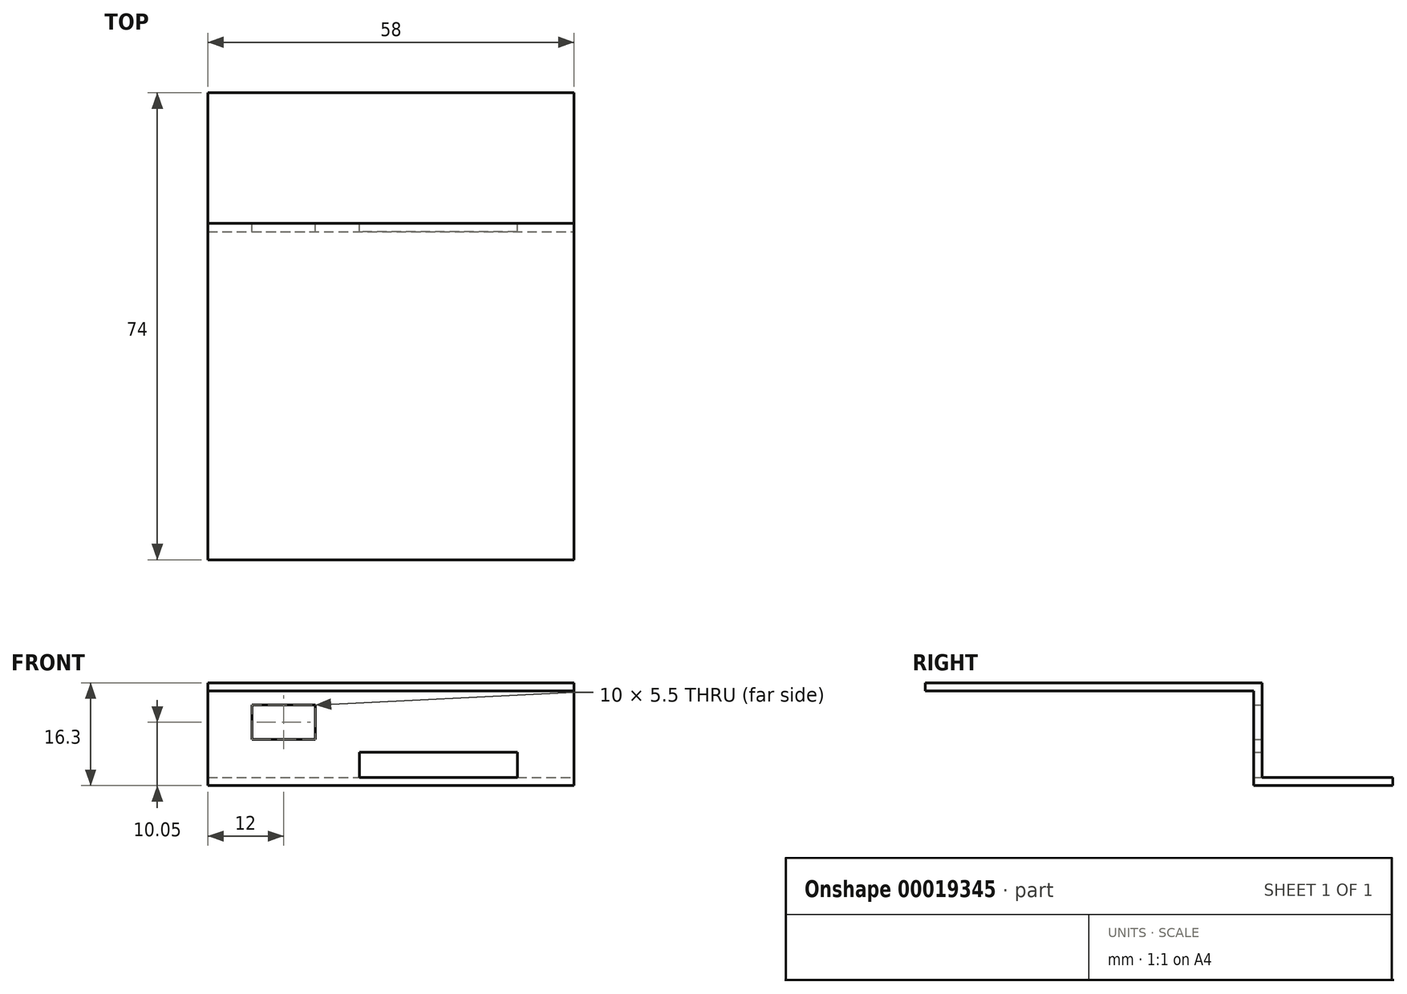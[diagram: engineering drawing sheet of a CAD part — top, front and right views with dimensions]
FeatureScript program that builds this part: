
annotation { "Feature Type Name" : "Feature", "Feature Type Description" : "" }
export const myFeature = defineFeature(function(context is Context, id is Id, definition is map)
    precondition{}
    {
        {
            var Q0;
            Q0=qCreatedBy(makeId("Top.planeOp"),FACE);
            var sketch = newSketch(context, id + "F0", { "sketchPlane" : qUnion([Q0])});
            skLineSegment(sketch, "E0.rect.bottom", {"start": v(27.5, 35.5) * mm, "end": v(-27.5, 35.5) * mm});
            skLineSegment(sketch, "E0.rect.top", {"start": v(27.5, -35.5) * mm, "end": v(-27.5, -35.5) * mm});
            skLineSegment(sketch, "E0.rect.left", {"start": v(27.5, 35.5) * mm, "end": v(27.5, -35.5) * mm});
            skLineSegment(sketch, "E0.rect.right", {"start": v(-27.5, 35.5) * mm, "end": v(-27.5, -35.5) * mm});
            skPoint(sketch, "E0.rect.middle", {"position": v(0, 0) * mm});
            skSolve(sketch);
        }
        {
            var Q0;
            Q0=qCreatedBy(makeId("Top.planeOp"),FACE);
            var sketch = newSketch(context, id + "F1", { "sketchPlane" : qUnion([Q0])});
            skLineSegment(sketch, "E1.0", {"start": v(29, -37) * mm, "end": v(29, 37) * mm});
            skLineSegment(sketch, "E1.1", {"start": v(-29, -37) * mm, "end": v(29, -37) * mm});
            skLineSegment(sketch, "E1.2", {"start": v(-29, 37) * mm, "end": v(-29, -37) * mm});
            skLineSegment(sketch, "E1.3", {"start": v(29, 37) * mm, "end": v(-29, 37) * mm});
            skSolve(sketch);
        }
        {
            var Q0;
            Q0=qSketchRegion(id+"F1",true);
            extrude(context, id + "F2", {"entities" : qUnion([Q0]), "depth" : 32 * mm});
        }
        {
            var Q0;
            Q0=makeQuery(id+"F2.opExtrude","CAP_FACE",FACE,{"disambiguationData":[OSD([sQuery(id+"F1.wireOp",EDGE,"E1.0"),sQuery(id+"F1.wireOp",EDGE,"E1.1"),sQuery(id+"F1.wireOp",EDGE,"E1.2"),sQuery(id+"F1.wireOp",EDGE,"E1.3")])],"isStart":false});
            var sketch = newSketch(context, id + "F3", { "sketchPlane" : qUnion([Q0])});
            skLineSegment(sketch, "E2.0", {"start": v(-27.5, -35.5) * mm, "end": v(27.5, -35.5) * mm});
            skLineSegment(sketch, "E2.1", {"start": v(-27.5, 35.5) * mm, "end": v(-27.5, -35.5) * mm});
            skLineSegment(sketch, "E2.2", {"start": v(27.5, 35.5) * mm, "end": v(-27.5, 35.5) * mm});
            skLineSegment(sketch, "E2.3", {"start": v(27.5, -35.5) * mm, "end": v(27.5, 35.5) * mm});
            skSolve(sketch);
        }
        {
            var Q0;
            Q0=qSketchRegion(id+"F3",true);
            extrude(context, id + "F4", {"entities" : qUnion([Q0]), "operationType" : NewBodyOperationType.REMOVE, "oppositeDirection" : true, "depth" : 31 * mm});
        }
        {
            var Q0;
            Q0=makeQuery(id+"F2.opExtrude","SWEPT_FACE",FACE,{"disambiguationData":[OSD([sQuery(id+"F1.wireOp",EDGE,"E1.3")])]});
            var sketch = newSketch(context, id + "F5", { "sketchPlane" : qUnion([Q0])});
            skLineSegment(sketch, "E3.rect.bottom", {"start": v(24, 5.5) * mm, "end": v(13, 5.5) * mm});
            skLineSegment(sketch, "E3.rect.top", {"start": v(24, 17) * mm, "end": v(13, 17) * mm});
            skLineSegment(sketch, "E3.rect.left", {"start": v(24, 5.5) * mm, "end": v(24, 17) * mm});
            skLineSegment(sketch, "E3.rect.right", {"start": v(13, 5.5) * mm, "end": v(13, 17) * mm});
            skPoint(sketch, "E3.rect.middle", {"position": v(18.5, 11.25) * mm});
            skLineSegment(sketch, "E4.rect.bottom", {"start": v(-5, 5.5) * mm, "end": v(-19, 5.5) * mm});
            skLineSegment(sketch, "E4.rect.top", {"start": v(-5, 17) * mm, "end": v(-19, 17) * mm});
            skLineSegment(sketch, "E4.rect.left", {"start": v(-5, 5.5) * mm, "end": v(-5, 17) * mm});
            skLineSegment(sketch, "E4.rect.right", {"start": v(-19, 5.5) * mm, "end": v(-19, 17) * mm});
            skPoint(sketch, "E4.rect.middle", {"position": v(-12, 11.25) * mm});
            skSolve(sketch);
        }
        {
            var Q0;
            Q0=qSketchRegion(id+"F5",true);
            extrude(context, id + "F6", {"entities" : qUnion([Q0]), "operationType" : NewBodyOperationType.REMOVE, "endBound" : BoundingType.UP_TO_NEXT, "oppositeDirection" : true, "depth" : 25 * mm});
        }
        {
            var Q0;
            Q0=makeQuery(id+"F2.opExtrude","SWEPT_FACE",FACE,{"disambiguationData":[OSD([sQuery(id+"F1.wireOp",EDGE,"E1.2")])]});
            var sketch = newSketch(context, id + "F7", { "sketchPlane" : qUnion([Q0])});
            skLineSegment(sketch, "E5.rect.bottom", {"start": v(-15, 17) * mm, "end": v(-37, 17) * mm});
            skLineSegment(sketch, "E5.rect.top", {"start": v(-15, 32) * mm, "end": v(-37, 32) * mm});
            skLineSegment(sketch, "E5.rect.left", {"start": v(-15, 17) * mm, "end": v(-15, 32) * mm});
            skLineSegment(sketch, "E5.rect.right", {"start": v(-37, 17) * mm, "end": v(-37, 32) * mm});
            skPoint(sketch, "E5.rect.middle", {"position": v(-26, 24.5) * mm});
            skSolve(sketch);
        }
        {
            var Q0;
            Q0=qSketchRegion(id+"F7",true);
            extrude(context, id + "F8", {"entities" : qUnion([Q0]), "operationType" : NewBodyOperationType.REMOVE, "endBound" : BoundingType.THROUGH_ALL, "oppositeDirection" : true, "depth" : 25 * mm});
        }
        {
            var Q0;
            Q0=makeQuery(id+"F4.boolean.opBoolean","COPY",FACE,{"derivedFrom":makeQuery(id+"F4.opExtrude","CAP_FACE",FACE,{"disambiguationData":[OSD([sQuery(id+"F3.wireOp",EDGE,"E2.0"),sQuery(id+"F3.wireOp",EDGE,"E2.1"),sQuery(id+"F3.wireOp",EDGE,"E2.2"),sQuery(id+"F3.wireOp",EDGE,"E2.3")])],"isStart":false})});
            var sketch = newSketch(context, id + "F9", { "sketchPlane" : qUnion([Q0])});
            skCircle(sketch, "E6", {"center": v(24.9, 20.2) * mm, "radius": 1.4 * mm});
            skCircle(sketch, "E7", {"center": v(7.36, -30.2) * mm, "radius": 1.4 * mm});
            skCircle(sketch, "E8", {"center": v(-17.64, -30.2) * mm, "radius": 1.4 * mm});
            skSolve(sketch);
        }
        {
            var Q0;
            Q0=qSketchRegion(id+"F9",true);
            extrude(context, id + "F10", {"entities" : qUnion([Q0]), "operationType" : NewBodyOperationType.ADD, "depth" : 6 * mm});
        }
        {
            var Q0;
            Q0=makeQuery(id+"F2.opExtrude","SWEPT_FACE",FACE,{"disambiguationData":[OSD([sQuery(id+"F1.wireOp",EDGE,"E1.0")])]});
            var sketch = newSketch(context, id + "F11", { "sketchPlane" : qUnion([Q0])});
            skLineSegment(sketch, "E9", {"start": v(-37, 32) * mm, "end": v(15, 32) * mm});
            skLineSegment(sketch, "E10", {"start": v(15, 32) * mm, "end": v(15, 17) * mm});
            skLineSegment(sketch, "E11", {"start": v(15, 17) * mm, "end": v(37, 17) * mm});
            skLineSegment(sketch, "E12.0", {"start": v(16.3, 18.3) * mm, "end": v(37, 18.3) * mm});
            skLineSegment(sketch, "E12.1", {"start": v(16.3, 33.3) * mm, "end": v(16.3, 18.3) * mm});
            skLineSegment(sketch, "E12.2", {"start": v(-37, 33.3) * mm, "end": v(16.3, 33.3) * mm});
            skLineSegment(sketch, "E13", {"start": v(-37, 33.3) * mm, "end": v(-37, 32) * mm});
            skLineSegment(sketch, "E14", {"start": v(37, 18.3) * mm, "end": v(37, 17) * mm});
            skSolve(sketch);
        }
        {
            var Q0;
            Q0 = qSketchRegion(id + "F11", true);
            var Q1;
            Q1=makeQuery(id+"F2.opExtrude","SWEPT_FACE",FACE,{"disambiguationData":[OSD([sQuery(id+"F1.wireOp",EDGE,"E1.2")])]});
            extrude(context, id + "F12", {"entities" : qUnion([Q0]), "endBound" : BoundingType.UP_TO_SURFACE, "oppositeDirection" : true, "endBoundEntityFace" : qUnion([Q1]), "depth" : 25 * mm});
        }
        {
            var Q0;
            Q0=makeQuery(id+"F12.opExtrude","SWEPT_FACE",FACE,{"disambiguationData":[OSD([sQuery(id+"F11.wireOp",EDGE,"E12.1")])]});
            var sketch = newSketch(context, id + "F13", { "sketchPlane" : qUnion([Q0])});
            skLineSegment(sketch, "E15.bottom", {"start": v(12, 29.8) * mm, "end": v(22, 29.8) * mm});
            skLineSegment(sketch, "E15.top", {"start": v(12, 24.3) * mm, "end": v(22, 24.3) * mm});
            skLineSegment(sketch, "E15.left", {"start": v(12, 29.8) * mm, "end": v(12, 24.3) * mm});
            skLineSegment(sketch, "E15.right", {"start": v(22, 29.8) * mm, "end": v(22, 24.3) * mm});
            skLineSegment(sketch, "E16.bottom", {"start": v(-20, 22.3) * mm, "end": v(5, 22.3) * mm});
            skLineSegment(sketch, "E16.top", {"start": v(-20, 18.3) * mm, "end": v(5, 18.3) * mm});
            skLineSegment(sketch, "E16.left", {"start": v(-20, 22.3) * mm, "end": v(-20, 18.3) * mm});
            skLineSegment(sketch, "E16.right", {"start": v(5, 22.3) * mm, "end": v(5, 18.3) * mm});
            skSolve(sketch);
        }
        {
            var Q0;
            Q0 = qSketchRegion(id + "F13", true);
            extrude(context, id + "F14", {"entities" : qUnion([Q0]), "operationType" : NewBodyOperationType.REMOVE, "endBound" : BoundingType.UP_TO_NEXT, "oppositeDirection" : true, "depth" : 25 * mm});
        }
        {
            var Q0;
            Q0=makeQuery(id+"F2.opExtrude","SWEPT_BODY",BODY,{"disambiguationData":[OSD([sQuery(id+"F1.wireOp",EDGE,"E1.0"),sQuery(id+"F1.wireOp",EDGE,"E1.1"),sQuery(id+"F1.wireOp",EDGE,"E1.2"),sQuery(id+"F1.wireOp",EDGE,"E1.3")])]});
            deleteBodies(context, id + "F15", {"entities" : qUnion([Q0])});
        }
    });
